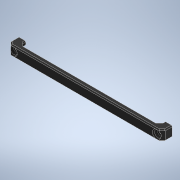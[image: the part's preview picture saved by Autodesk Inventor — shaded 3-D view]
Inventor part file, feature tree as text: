
AUTODESK INVENTOR PART (.ipt)
format: ipt  version: 2021 (Build 250183000, 183)  size: 288,256 bytes
history: native  units: mm
features: extrude x7, sketch x7, chamfer x7, plane x3, thicken_offset x2, mirror x1, projected_geometry x1
ambient origin geometry x8: Origin, YZ Plane, XZ Plane, XY Plane, X Axis, Y Axis, Z Axis, Center Point
bodies: Solid1 (feature_tree)
feature tree (28):
  extrude  "Extrusion1"  Depth=10.0mm
  extrude  "Extrusion2"  Depth=67.5mm
  extrude  "Extrusion3"  Depth=5.0mm
  sketch  "Sketch4"  dims[d10=0.0mm d11=0.0mm d12=1.6mm]
  plane  "Work Plane1"
  extrude  "Extrusion5"  Depth=1.6mm
  extrude  "Extrusion6"  Depth=5.6mm
  sketch  "Sketch6"  dims[d21=2.0mm d22=3.75mm d23=0.0mm d25=5.3mm d27=0.0mm d28=0.0mm]
  plane  "Work Plane2"
  extrude  "Extrusion7"  Depth=5.3mm
  mirror  "Mirror1"
  chamfer  "Chamfer3"  [1 undecoded]
  chamfer  "Chamfer5"  Distance=3.75mm
  chamfer  "Chamfer6"  Distance=2.0mm
  extrude  "Extrusion8"  Depth=3.0mm
  chamfer  "Chamfer7"  Distance=2.8mm
  chamfer  "Chamfer8"  Distance=5.6mm
  thicken_offset  "Thicken1"
  thicken_offset  "Thicken2"
  chamfer  "Chamfer9"  Distance=1.0mm Angle=45.0deg
  chamfer  "Chamfer10"  Distance=1.0mm Angle=45.0deg
  sketch  "Sketch1"  dims[d0=150.0mm d1=10.0mm]
  sketch  "Sketch2"  dims[d2=10.0mm d3=0.0mm d7=67.5mm]
  sketch  "Sketch3"  dims[d8=135.0mm d9=5.0mm]
  sketch  "Sketch5"  dims[d13=2.0mm d14=0.0mm d18=5.6mm]
  projected_geometry  "Projected Loop1"
  plane  "Work Plane3"
  sketch  "Sketch7"  dims[d29=-2.0mm d30=3.75mm d31=0.0mm d32=2.0mm d33=3.0mm d34=2.8mm d35=5.6mm d39=1.0mm d40=2.0mm d41=45.0deg d45=1.0mm d46=2.0mm d47=45.0deg d48=70.0mm d49=1.9mm d50=2.0mm d51=45.0deg d52=0.0mm d53=0.0mm d54=1.0mm d55=2.0mm d56=45.0deg d57=0.5mm d58=2.0mm d59=45.0deg d60=0.2mm d61=0.2mm d62=0.2mm d63=0.2mm d64=3.0mm d65=2.0mm d66=45.0deg d67=1.0mm d68=2.0mm d69=45.0deg d70=6.5mm]
note: 1 required parameter value undecoded (feature->parameter linkage not recoverable at this tier; creation-order binding heuristic only, values carry confidence <= 0.55)
